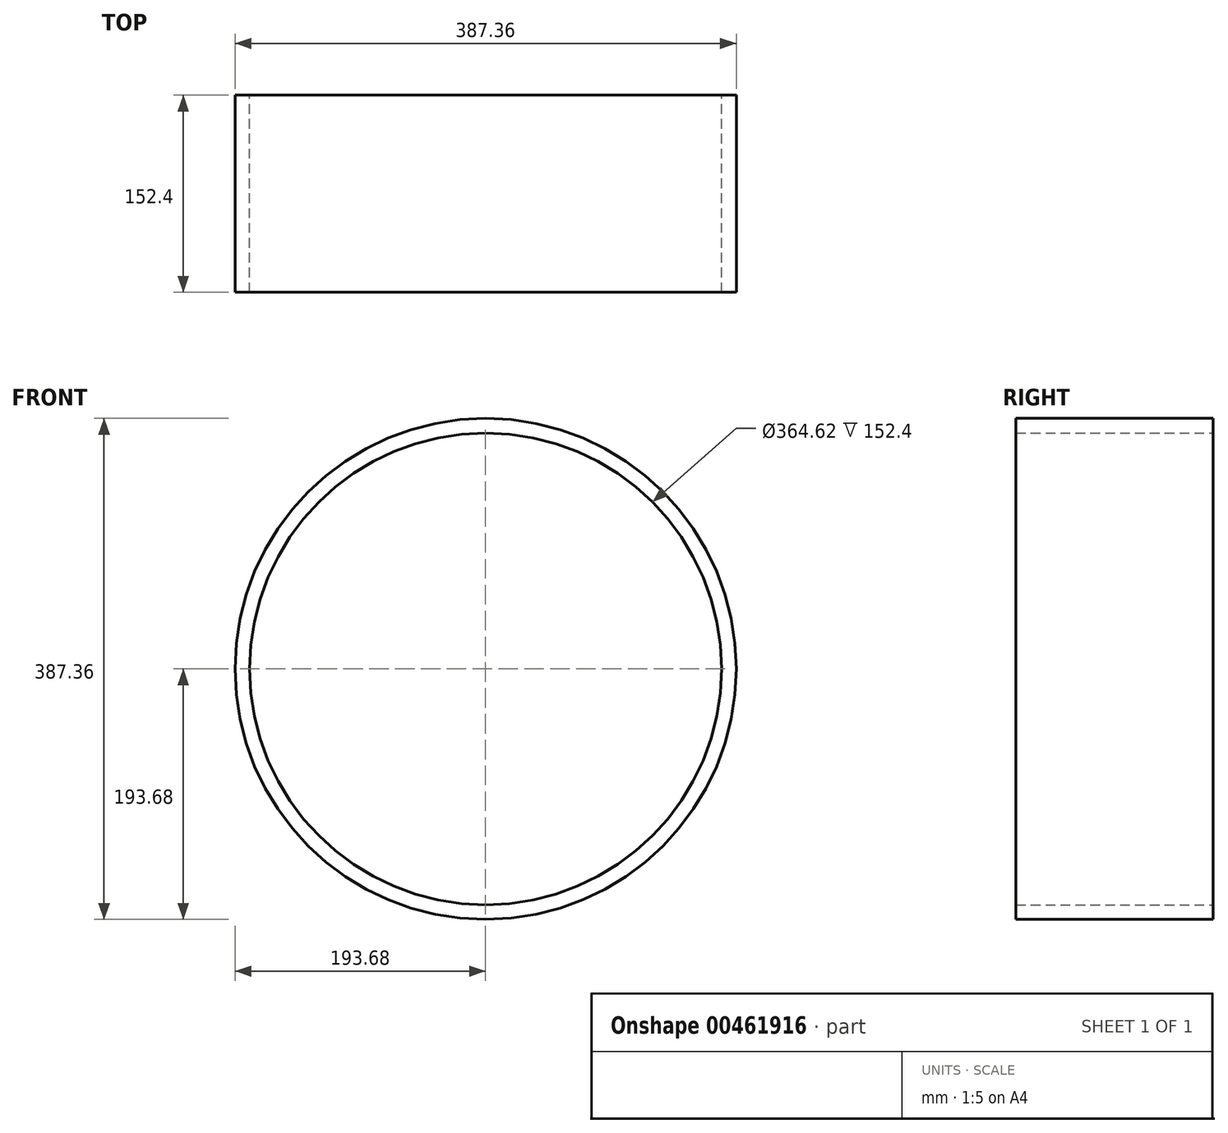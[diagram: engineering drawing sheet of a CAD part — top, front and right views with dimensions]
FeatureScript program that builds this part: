
annotation { "Feature Type Name" : "Feature", "Feature Type Description" : "" }
export const myFeature = defineFeature(function(context is Context, id is Id, definition is map)
    precondition{}
    {
        {
            var Q0;
            Q0=qCreatedBy(makeId("Front.planeOp"),FACE);
            var sketch = newSketch(context, id + "F0", { "sketchPlane" : qUnion([Q0])});
            skCircle(sketch, "E0", {"center": v(0, 0) * mm, "radius": 193.68 * mm});
            skCircle(sketch, "E1", {"center": v(0, 0) * mm, "radius": 182.3 * mm});
            skSolve(sketch);
        }
        {
            var Q0;
            Q0 = qSketchRegion(id + "F0", true);
            extrude(context, id + "F1", {"entities" : qUnion([Q0]), "endBound" : BoundingType.SYMMETRIC, "depth" : 152.4 * mm});
        }
    });
